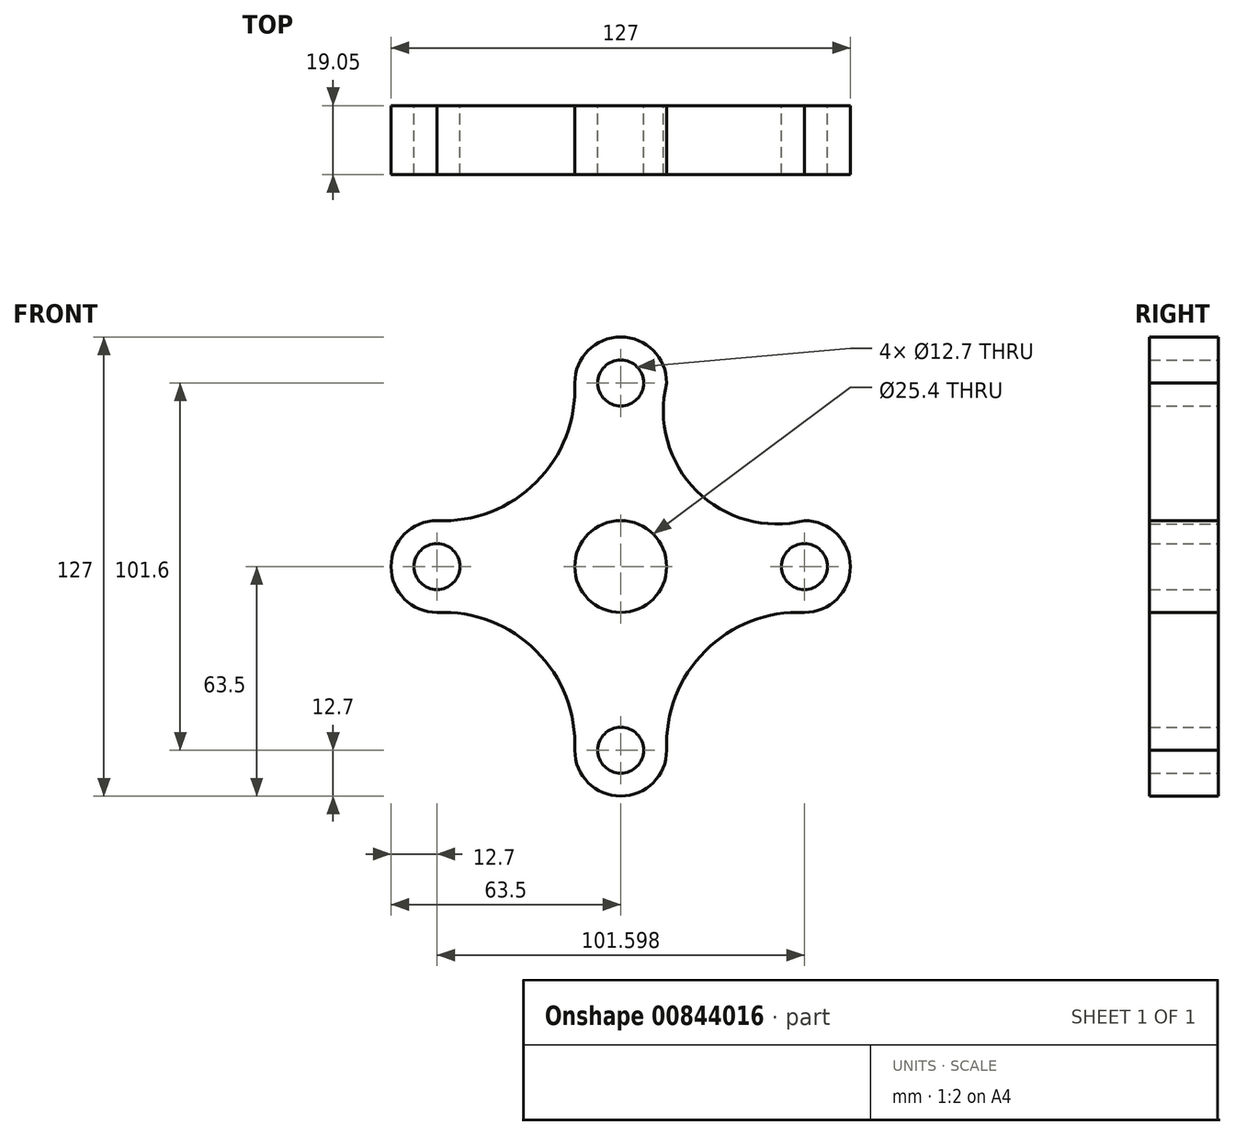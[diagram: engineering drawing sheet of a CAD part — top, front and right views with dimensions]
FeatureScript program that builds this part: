
annotation { "Feature Type Name" : "Feature", "Feature Type Description" : "" }
export const myFeature = defineFeature(function(context is Context, id is Id, definition is map)
    precondition{}
    {
        {
            var Q0;
            Q0=qCreatedBy(makeId("Front.planeOp"),FACE);
            var sketch = newSketch(context, id + "F0", { "sketchPlane" : qUnion([Q0])});
            skCircle(sketch, "E0", {"center": v(0, 0) * mm, "radius": 12.7 * mm});
            skCircle(sketch, "E1", {"center": v(50.8, 0) * mm, "radius": 6.35 * mm});
            skCircle(sketch, "E2", {"center": v(0, 50.8) * mm, "radius": 6.35 * mm});
            skCircle(sketch, "E3", {"center": v(-50.8, 0) * mm, "radius": 6.35 * mm});
            skCircle(sketch, "E4", {"center": v(0, -50.8) * mm, "radius": 6.35 * mm});
            skArc(sketch, "E5", {"start": v(-50.8, -12.7) * mm, "mid": v(-63.5, 0) * mm, "end": v(-50.8, 12.7) * mm});
            skArc(sketch, "E6", {"start": v(-12.7, 50.8) * mm, "mid": v(0, 63.5) * mm, "end": v(12.7, 50.8) * mm});
            skArc(sketch, "E7", {"start": v(50.8, 12.7) * mm, "mid": v(63.5, 0) * mm, "end": v(50.8, -12.7) * mm});
            skArc(sketch, "E8", {"start": v(12.7, -50.8) * mm, "mid": v(0, -63.5) * mm, "end": v(-12.7, -50.8) * mm});
            skArc(sketch, "E9", {"start": v(-50.8, 12.7) * mm, "mid": v(-23.36, 23.36) * mm, "end": v(-12.7, 50.8) * mm});
            skArc(sketch, "E10", {"start": v(12.7, 50.8) * mm, "mid": v(20.96, 20.97) * mm, "end": v(50.8, 12.7) * mm});
            skArc(sketch, "E11", {"start": v(50.8, -12.7) * mm, "mid": v(23.36, -23.36) * mm, "end": v(12.7, -50.8) * mm});
            skArc(sketch, "E12", {"start": v(-12.7, -50.8) * mm, "mid": v(-23.36, -23.36) * mm, "end": v(-50.8, -12.7) * mm});
            skSolve(sketch);
        }
        {
            var Q0;
            Q0=makeQuery(id+"F0.imprint","IMPRINT",FACE,{"disambiguationData":[TD([[makeQuery(id+"F0.imprint","IMPRINT",EDGE,{"derivedFrom":sQuery(id+"F0.wireOp",EDGE,"E0")}),-1.0]])]});
            extrude(context, id + "F1", {"entities" : qUnion([Q0]), "depth" : 19.05 * mm, "offsetDistance" : 25.4 * mm});
        }
    });
